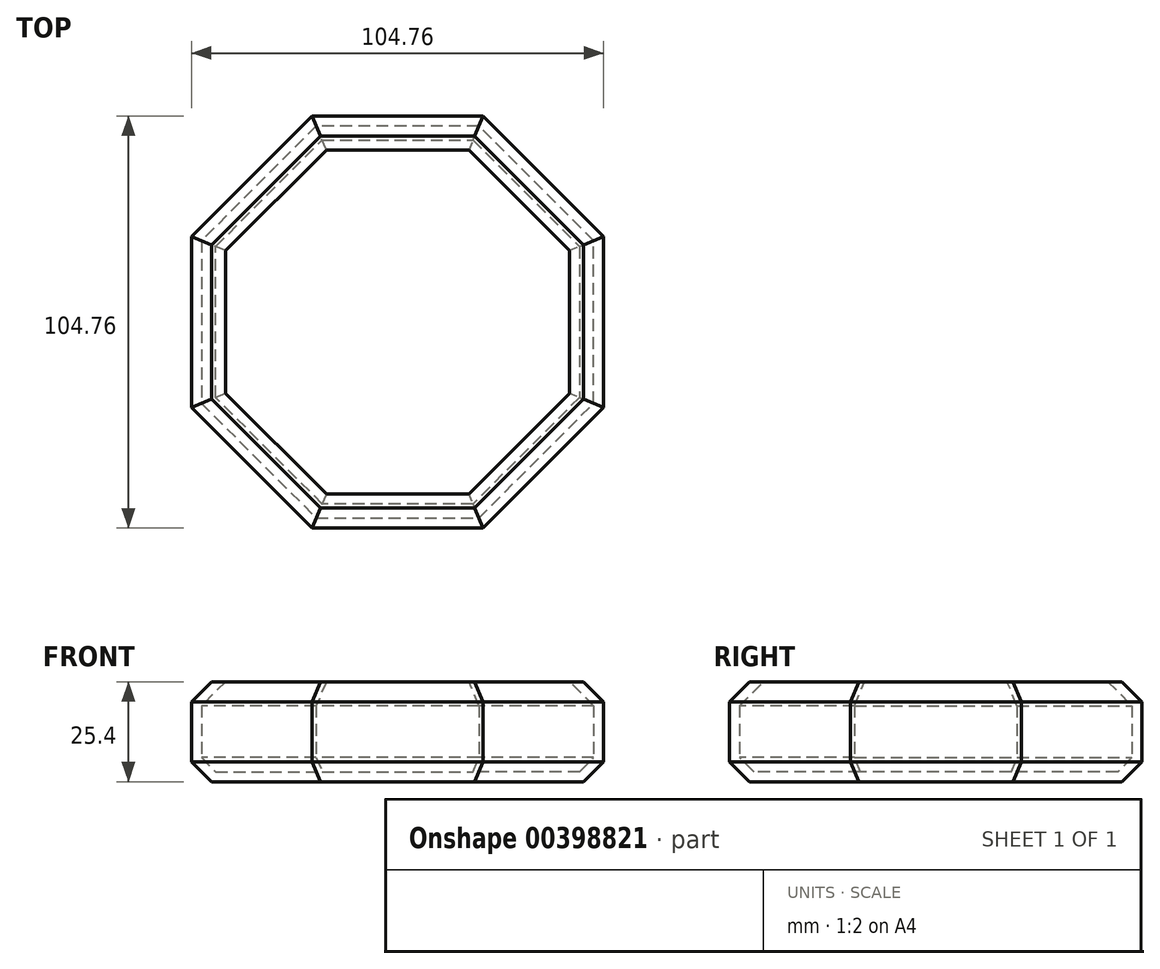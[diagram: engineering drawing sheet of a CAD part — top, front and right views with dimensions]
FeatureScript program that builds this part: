
annotation { "Feature Type Name" : "Feature", "Feature Type Description" : "" }
export const myFeature = defineFeature(function(context is Context, id is Id, definition is map)
    precondition{}
    {
        {
            var Q0;
            Q0=qCreatedBy(makeId("Top.planeOp"),FACE);
            var sketch = newSketch(context, id + "F0", { "sketchPlane" : qUnion([Q0])});
            skCircle(sketch, "E0.cCircle", {"center": v(0, 0) * mm, "radius": 52.38 * mm, "construction": true});
            skLineSegment(sketch, "E0.0", {"start": v(52.38, 21.7) * mm, "end": v(52.38, -21.7) * mm});
            skLineSegment(sketch, "E0.1", {"start": v(52.38, -21.7) * mm, "end": v(21.7, -52.38) * mm});
            skLineSegment(sketch, "E0.2", {"start": v(21.7, -52.38) * mm, "end": v(-21.7, -52.38) * mm});
            skLineSegment(sketch, "E0.3", {"start": v(-21.7, -52.38) * mm, "end": v(-52.38, -21.7) * mm});
            skLineSegment(sketch, "E0.4", {"start": v(-52.38, -21.7) * mm, "end": v(-52.38, 21.7) * mm});
            skLineSegment(sketch, "E0.5", {"start": v(-52.38, 21.7) * mm, "end": v(-21.7, 52.38) * mm});
            skLineSegment(sketch, "E0.6", {"start": v(-21.7, 52.38) * mm, "end": v(21.7, 52.38) * mm});
            skLineSegment(sketch, "E0.7", {"start": v(21.7, 52.38) * mm, "end": v(52.38, 21.7) * mm});
            skPoint(sketch, "E0.0.midPoint", {"position": v(52.38, 0) * mm});
            skSolve(sketch);
        }
        {
            var Q0;
            Q0=makeQuery(id+"F0.imprint","IMPRINT",FACE,{"disambiguationData":[TD([[makeQuery(id+"F0.imprint","IMPRINT",EDGE,{"derivedFrom":sQuery(id+"F0.wireOp",EDGE,"E0.0")}),-1.0]])]});
            extrude(context, id + "F1", {"entities" : qUnion([Q0]), "depth" : 25.4 * mm});
        }
        {
            var Q0;
            Q0=makeQuery(id+"F1.opExtrude","CAP_FACE",FACE,{"disambiguationData":[OSD([sQuery(id+"F0.wireOp",EDGE,"E0.0"),sQuery(id+"F0.wireOp",EDGE,"E0.1"),sQuery(id+"F0.wireOp",EDGE,"E0.2"),sQuery(id+"F0.wireOp",EDGE,"E0.3"),sQuery(id+"F0.wireOp",EDGE,"E0.4"),sQuery(id+"F0.wireOp",EDGE,"E0.5"),sQuery(id+"F0.wireOp",EDGE,"E0.6"),sQuery(id+"F0.wireOp",EDGE,"E0.7")])],"isStart":false});
            var Q1;
            Q1=makeQuery(id+"F1.opExtrude","CAP_FACE",FACE,{"disambiguationData":[OSD([sQuery(id+"F0.wireOp",EDGE,"E0.0"),sQuery(id+"F0.wireOp",EDGE,"E0.1"),sQuery(id+"F0.wireOp",EDGE,"E0.2"),sQuery(id+"F0.wireOp",EDGE,"E0.3"),sQuery(id+"F0.wireOp",EDGE,"E0.4"),sQuery(id+"F0.wireOp",EDGE,"E0.5"),sQuery(id+"F0.wireOp",EDGE,"E0.6"),sQuery(id+"F0.wireOp",EDGE,"E0.7")])],"isStart":true});
            chamfer(context, id + "F2", {"entities" : qUnion([Q0, Q1]), "width" : 5.08 * mm, "tangentPropagation" : true});
        }
        {
            var Q0;
            Q0=makeQuery(id+"F1.opExtrude","CAP_FACE",FACE,{"disambiguationData":[OSD([sQuery(id+"F0.wireOp",EDGE,"E0.0"),sQuery(id+"F0.wireOp",EDGE,"E0.1"),sQuery(id+"F0.wireOp",EDGE,"E0.2"),sQuery(id+"F0.wireOp",EDGE,"E0.3"),sQuery(id+"F0.wireOp",EDGE,"E0.4"),sQuery(id+"F0.wireOp",EDGE,"E0.5"),sQuery(id+"F0.wireOp",EDGE,"E0.6"),sQuery(id+"F0.wireOp",EDGE,"E0.7")])],"isStart":false});
            shell(context, id + "F3", {"entities" : qUnion([Q0]), "thickness" : 2.54 * mm});
        }
    });
